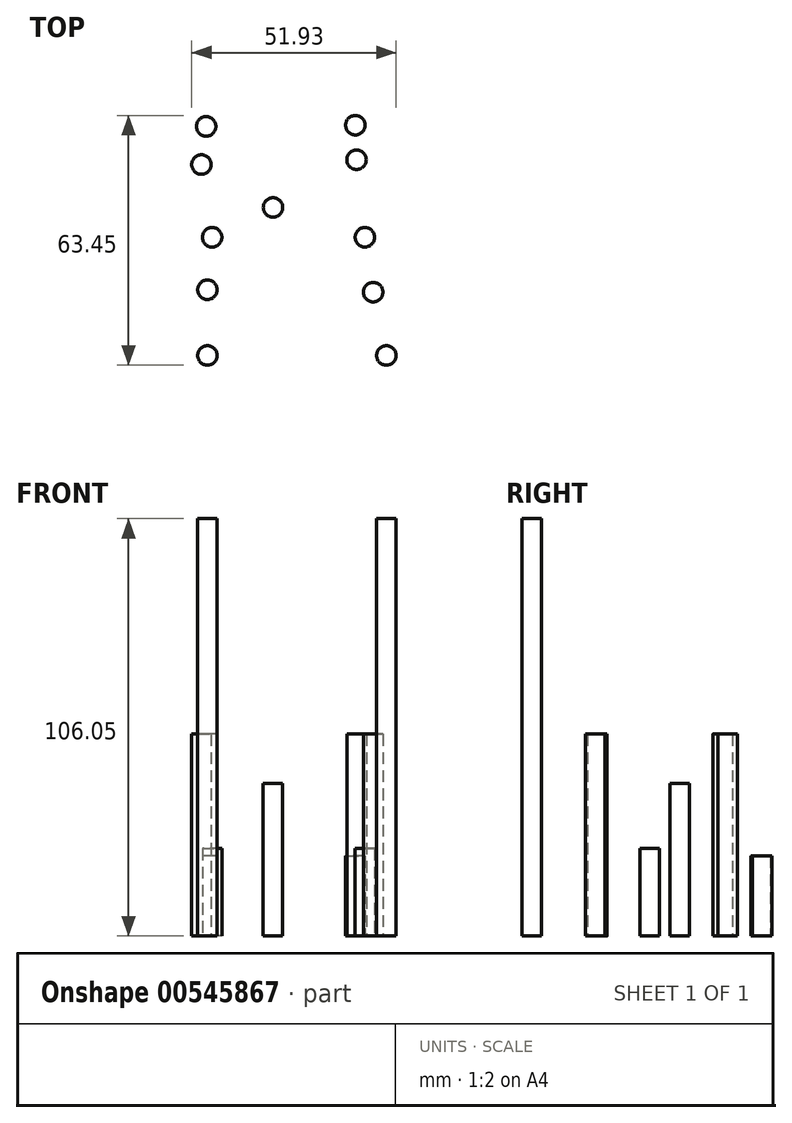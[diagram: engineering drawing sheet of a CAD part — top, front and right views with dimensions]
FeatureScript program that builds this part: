
annotation { "Feature Type Name" : "Feature", "Feature Type Description" : "" }
export const myFeature = defineFeature(function(context is Context, id is Id, definition is map)
    precondition{}
    {
        {
            var Q0;
            Q0=qCreatedBy(makeId("Top.planeOp"),FACE);
            var sketch = newSketch(context, id + "F0", { "sketchPlane" : qUnion([Q0])});
            skCircle(sketch, "E0", {"center": v(-22.12, 0) * mm, "radius": 2.48 * mm});
            skCircle(sketch, "E1", {"center": v(23.34, 0) * mm, "radius": 2.48 * mm});
            skSolve(sketch);
        }
        {
            var Q0;
            Q0=qSketchRegion(id+"F0",true);
            extrude(context, id + "F1", {"entities" : qUnion([Q0]), "depth" : 106.04 * mm, "offsetDistance" : 25.4 * mm});
        }
        {
            var Q0;
            Q0=qCreatedBy(makeId("Top.planeOp"),FACE);
            var sketch = newSketch(context, id + "F2", { "sketchPlane" : qUnion([Q0])});
            skCircle(sketch, "E2", {"center": v(-22.12, 16.67) * mm, "radius": 2.48 * mm});
            skCircle(sketch, "E3", {"center": v(20, 16.06) * mm, "radius": 2.48 * mm});
            skSolve(sketch);
        }
        {
            var Q0;
            Q0=qSketchRegion(id+"F2",true);
            extrude(context, id + "F3", {"entities" : qUnion([Q0]), "depth" : 51.3 * mm, "offsetDistance" : 25.4 * mm});
        }
        {
            var Q0;
            Q0=qCreatedBy(makeId("Top.planeOp"),FACE);
            var sketch = newSketch(context, id + "F4", { "sketchPlane" : qUnion([Q0])});
            skCircle(sketch, "E4", {"center": v(-20.91, 30) * mm, "radius": 2.48 * mm});
            skCircle(sketch, "E5", {"center": v(17.88, 30) * mm, "radius": 2.48 * mm});
            skSolve(sketch);
        }
        {
            var Q0;
            Q0=makeQuery(id+"F4.imprint","IMPRINT",FACE,{"disambiguationData":[TD([[makeQuery(id+"F4.imprint","IMPRINT",EDGE,{"derivedFrom":sQuery(id+"F4.wireOp",EDGE,"E4")}),1.0]])]});
            var Q1;
            Q1=makeQuery(id+"F4.imprint","IMPRINT",FACE,{"disambiguationData":[TD([[makeQuery(id+"F4.imprint","IMPRINT",EDGE,{"derivedFrom":sQuery(id+"F4.wireOp",EDGE,"E5")}),1.0]])]});
            extrude(context, id + "F5", {"entities" : qUnion([Q0, Q1]), "depth" : 22.22 * mm, "offsetDistance" : 25.4 * mm});
        }
        {
            var Q0;
            Q0=qCreatedBy(makeId("Top.planeOp"),FACE);
            var sketch = newSketch(context, id + "F6", { "sketchPlane" : qUnion([Q0])});
            skCircle(sketch, "E6", {"center": v(-5.46, 37.58) * mm, "radius": 2.48 * mm});
            skSolve(sketch);
        }
        {
            var Q0;
            Q0=makeQuery(id+"F6.imprint","IMPRINT",FACE,{"disambiguationData":[TD([[makeQuery(id+"F6.imprint","IMPRINT",EDGE,{"derivedFrom":sQuery(id+"F6.wireOp",EDGE,"E6")}),1.0]])]});
            extrude(context, id + "F7", {"entities" : qUnion([Q0]), "depth" : 38.73 * mm, "offsetDistance" : 25.4 * mm});
        }
        {
            var Q0;
            Q0=qCreatedBy(makeId("Top.planeOp"),FACE);
            var sketch = newSketch(context, id + "F8", { "sketchPlane" : qUnion([Q0])});
            skCircle(sketch, "E7", {"center": v(-23.64, 48.5) * mm, "radius": 2.48 * mm});
            skCircle(sketch, "E8", {"center": v(15.76, 49.7) * mm, "radius": 2.48 * mm});
            skSolve(sketch);
        }
        {
            var Q0;
            Q0=makeQuery(id+"F8.imprint","IMPRINT",FACE,{"disambiguationData":[TD([[makeQuery(id+"F8.imprint","IMPRINT",EDGE,{"derivedFrom":sQuery(id+"F8.wireOp",EDGE,"E7")}),1.0]])]});
            var Q1;
            Q1=makeQuery(id+"F8.imprint","IMPRINT",FACE,{"disambiguationData":[TD([[makeQuery(id+"F8.imprint","IMPRINT",EDGE,{"derivedFrom":sQuery(id+"F8.wireOp",EDGE,"E8")}),1.0]])]});
            extrude(context, id + "F9", {"entities" : qUnion([Q0, Q1]), "depth" : 51.3 * mm, "offsetDistance" : 25.4 * mm});
        }
        {
            var Q0;
            Q0=qCreatedBy(makeId("Top.planeOp"),FACE);
            var sketch = newSketch(context, id + "F10", { "sketchPlane" : qUnion([Q0])});
            skCircle(sketch, "E9", {"center": v(-22.43, 58.19) * mm, "radius": 2.48 * mm});
            skCircle(sketch, "E10", {"center": v(15.46, 58.5) * mm, "radius": 2.48 * mm});
            skSolve(sketch);
        }
        {
            var Q0;
            Q0=makeQuery(id+"F10.imprint","IMPRINT",FACE,{"disambiguationData":[TD([[makeQuery(id+"F10.imprint","IMPRINT",EDGE,{"derivedFrom":sQuery(id+"F10.wireOp",EDGE,"E9")}),1.0]])]});
            var Q1;
            Q1=makeQuery(id+"F10.imprint","IMPRINT",FACE,{"disambiguationData":[TD([[makeQuery(id+"F10.imprint","IMPRINT",EDGE,{"derivedFrom":sQuery(id+"F10.wireOp",EDGE,"E10")}),1.0]])]});
            extrude(context, id + "F11", {"entities" : qUnion([Q0, Q1]), "depth" : 20.32 * mm, "offsetDistance" : 25.4 * mm});
        }
    });
